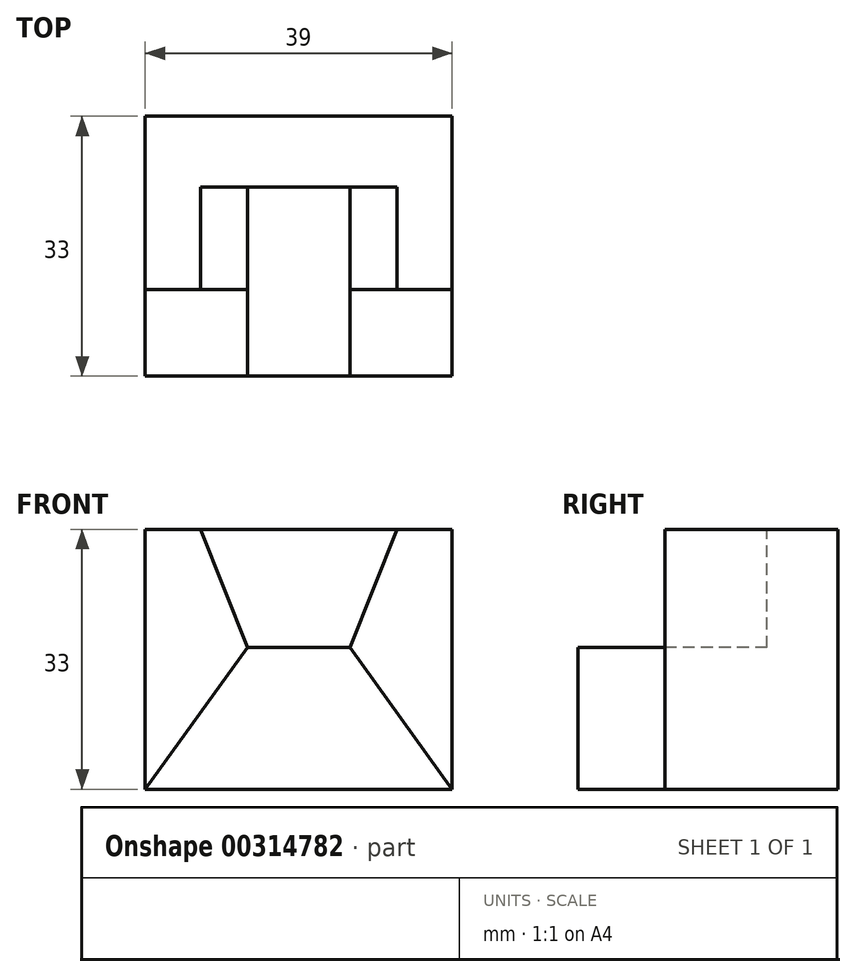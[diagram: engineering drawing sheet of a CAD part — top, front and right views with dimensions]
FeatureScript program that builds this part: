
annotation { "Feature Type Name" : "Feature", "Feature Type Description" : "" }
export const myFeature = defineFeature(function(context is Context, id is Id, definition is map)
    precondition{}
    {
        {
            var Q0;
            Q0=qCreatedBy(makeId("Front.planeOp"),FACE);
            var sketch = newSketch(context, id + "F0", { "sketchPlane" : qUnion([Q0])});
            skLineSegment(sketch, "E0.bottom", {"start": v(0, 0) * mm, "end": v(39, 0) * mm});
            skLineSegment(sketch, "E0.top", {"start": v(0, 33) * mm, "end": v(39, 33) * mm});
            skLineSegment(sketch, "E0.left", {"start": v(0, 0) * mm, "end": v(0, 33) * mm});
            skLineSegment(sketch, "E0.right", {"start": v(39, 0) * mm, "end": v(39, 33) * mm});
            skLineSegment(sketch, "E1", {"start": v(0, 0) * mm, "end": v(13, 18) * mm});
            skLineSegment(sketch, "E2", {"start": v(13, 18) * mm, "end": v(7, 33) * mm});
            skLineSegment(sketch, "E3", {"start": v(13, 18) * mm, "end": v(26, 18) * mm});
            skLineSegment(sketch, "E4", {"start": v(26, 18) * mm, "end": v(32, 33) * mm});
            skLineSegment(sketch, "E5", {"start": v(26, 18) * mm, "end": v(39, 0) * mm});
            skSolve(sketch);
        }
        {
            var Q0;
            Q0 = qSketchRegion(id + "F0", true);
            extrude(context, id + "F1", {"entities" : qUnion([Q0]), "oppositeDirection" : true, "depth" : 33 * mm});
        }
        {
            var Q0;
            {var subQ0=sQuery(id+"F0.wireOp",EDGE,"E0.left");Q0=makeQuery(id+"F0.imprint","IMPRINT",FACE,{"disambiguationData":[TD([[makeQuery(id+"F0.imprint","IMPRINT",EDGE,{"derivedFrom":subQ0}),-1.0]])]});}
            var Q1;
            {var subQ0=sQuery(id+"F0.wireOp",EDGE,"E2");Q1=makeQuery(id+"F0.imprint","IMPRINT",FACE,{"disambiguationData":[TD([[makeQuery(id+"F0.imprint","IMPRINT",EDGE,{"derivedFrom":subQ0}),-1.0]])]});}
            var Q2;
            {var subQ0=sQuery(id+"F0.wireOp",EDGE,"E0.right");Q2=makeQuery(id+"F0.imprint","IMPRINT",FACE,{"disambiguationData":[TD([[makeQuery(id+"F0.imprint","IMPRINT",EDGE,{"derivedFrom":subQ0}),1.0]])]});}
            extrude(context, id + "F2", {"entities" : qUnion([Q0, Q1, Q2]), "operationType" : NewBodyOperationType.REMOVE, "oppositeDirection" : true, "depth" : 11 * mm});
        }
        {
            var Q0;
            {var subQ0=sQuery(id+"F0.wireOp",EDGE,"E2");Q0=makeQuery(id+"F0.imprint","IMPRINT",FACE,{"disambiguationData":[TD([[makeQuery(id+"F0.imprint","IMPRINT",EDGE,{"derivedFrom":subQ0}),-1.0]])]});}
            extrude(context, id + "F3", {"entities" : qUnion([Q0]), "operationType" : NewBodyOperationType.REMOVE, "oppositeDirection" : true, "depth" : 24 * mm});
        }
    });
